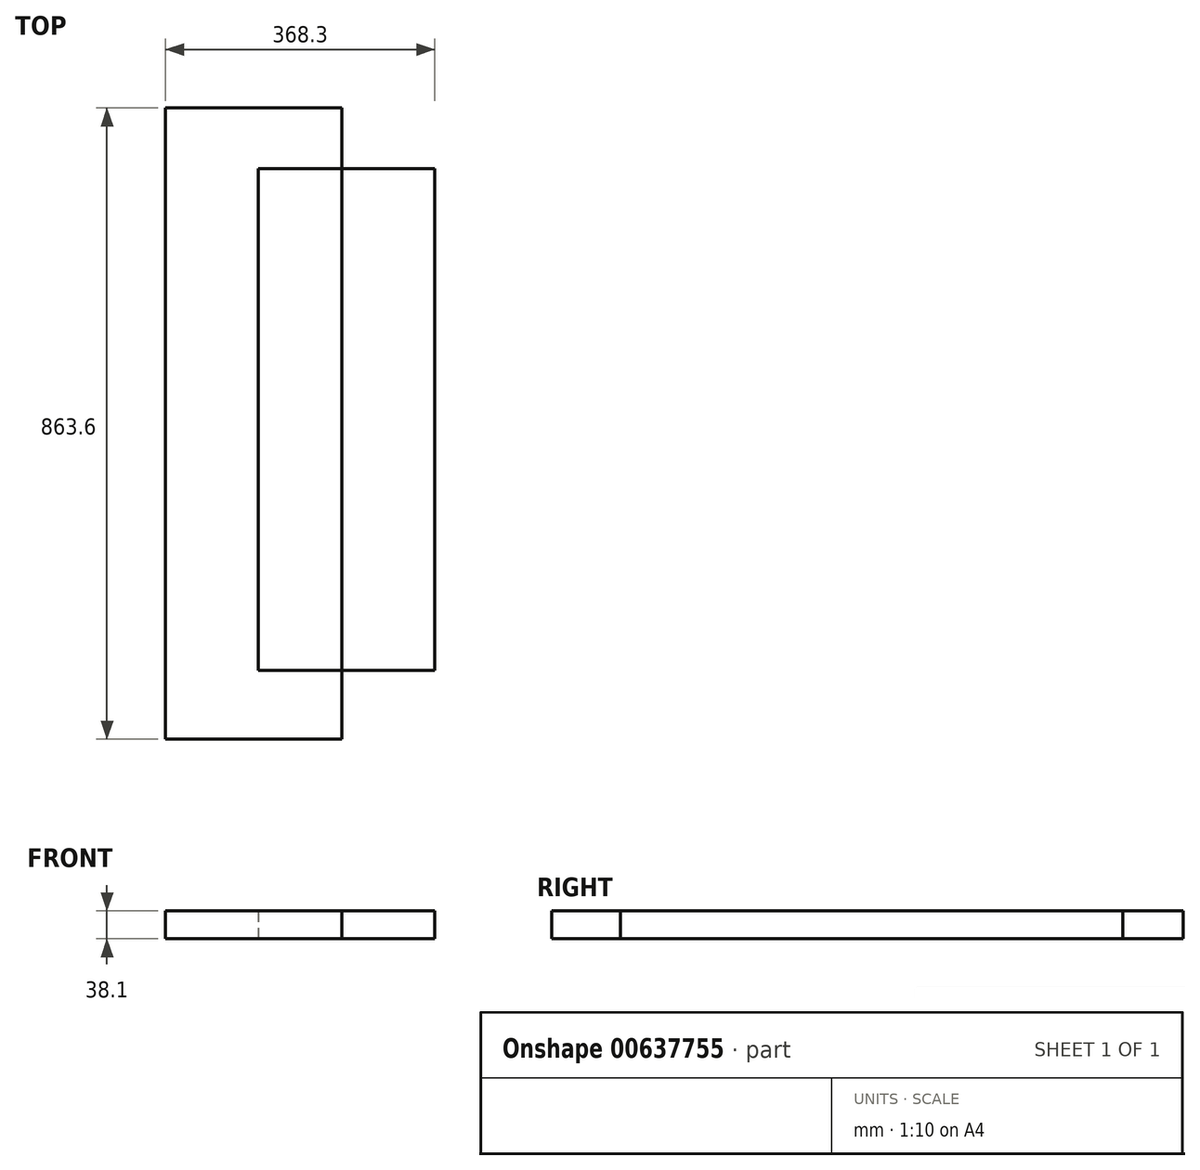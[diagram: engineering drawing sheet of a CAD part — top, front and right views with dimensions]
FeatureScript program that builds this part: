
annotation { "Feature Type Name" : "Feature", "Feature Type Description" : "" }
export const myFeature = defineFeature(function(context is Context, id is Id, definition is map)
    precondition{}
    {
        {
            var Q0;
            Q0=qCreatedBy(makeId("Top.planeOp"),FACE);
            var sketch = newSketch(context, id + "F0", { "sketchPlane" : qUnion([Q0])});
            skLineSegment(sketch, "E0.bottom", {"start": v(-122.87, 430.6) * mm, "end": v(4.13, 430.6) * mm});
            skLineSegment(sketch, "E0.top", {"start": v(-122.87, -433) * mm, "end": v(4.13, -433) * mm});
            skLineSegment(sketch, "E0.left", {"start": v(-122.87, 430.6) * mm, "end": v(-122.87, -433) * mm});
            skLineSegment(sketch, "E0.right", {"start": v(4.13, 430.6) * mm, "end": v(4.13, -433) * mm});
            skLineSegment(sketch, "E1.bottom", {"start": v(-122.87, -433) * mm, "end": v(245.43, -433) * mm});
            skLineSegment(sketch, "E1.top", {"start": v(-122.87, -339.02) * mm, "end": v(245.43, -339.02) * mm});
            skLineSegment(sketch, "E1.left", {"start": v(-122.87, -433) * mm, "end": v(-122.87, -339.02) * mm});
            skLineSegment(sketch, "E1.right", {"start": v(245.43, -433) * mm, "end": v(245.43, -339.02) * mm});
            skLineSegment(sketch, "E2.bottom", {"start": v(245.43, -433) * mm, "end": v(118.43, -433) * mm});
            skLineSegment(sketch, "E2.top", {"start": v(245.43, 430.6) * mm, "end": v(118.43, 430.6) * mm});
            skLineSegment(sketch, "E2.left", {"start": v(245.43, -433) * mm, "end": v(245.43, 430.6) * mm});
            skLineSegment(sketch, "E2.right", {"start": v(118.43, -433) * mm, "end": v(118.43, 430.6) * mm});
            skLineSegment(sketch, "E3.bottom", {"start": v(-122.87, 430.6) * mm, "end": v(245.43, 430.6) * mm});
            skLineSegment(sketch, "E3.top", {"start": v(-122.87, 347.87) * mm, "end": v(245.43, 347.87) * mm});
            skLineSegment(sketch, "E3.left", {"start": v(-122.87, 430.6) * mm, "end": v(-122.87, 347.87) * mm});
            skLineSegment(sketch, "E3.right", {"start": v(245.43, 430.6) * mm, "end": v(245.43, 347.87) * mm});
            skSolve(sketch);
        }
        {
            var Q0;
            {var subQ0=sQuery(id+"F0.wireOp",EDGE,"E0.left");Q0=makeQuery(id+"F0.imprint","IMPRINT",FACE,{"disambiguationData":[TD([[makeQuery(id+"F0.imprint","IMPRINT",EDGE,{"derivedFrom":subQ0}),1.0]])]});}
            var Q1;
            {var subQ5=sQuery(id+"F0.wireOp",EDGE,"E1.left");Q1=makeQuery(id+"F0.imprint","IMPRINT",FACE,{"disambiguationData":[TD([[makeQuery(id+"F0.imprint","IMPRINT",EDGE,{"derivedFrom":subQ5}),-1.0]])]});}
            var Q2;
            {var subQ0=sQuery(id+"F0.wireOp",EDGE,"E1.bottom");var subQ1=sQuery(id+"F0.wireOp",EDGE,"E0.right");var subQ2=makeQuery(id+"F0.imprint","INTERSECT",VERTEX,{"derivedFrom":[subQ1,subQ0]});Q2=makeQuery(id+"F0.imprint","IMPRINT",FACE,{"disambiguationData":[TD([[makeQuery(id+"F0.imprint","IMPRINT",EDGE,{"disambiguationData":[TD([[subQ2,1.0]])],"derivedFrom":subQ1}),1.0]])]});}
            var Q3;
            {var subQ5=sQuery(id+"F0.wireOp",EDGE,"E2.bottom");Q3=makeQuery(id+"F0.imprint","IMPRINT",FACE,{"disambiguationData":[TD([[makeQuery(id+"F0.imprint","IMPRINT",EDGE,{"derivedFrom":subQ5}),-1.0]])]});}
            var Q4;
            {var subQ0=sQuery(id+"F0.wireOp",EDGE,"E2.left");var subQ1=sQuery(id+"F0.wireOp",EDGE,"E1.top");var subQ2=makeQuery(id+"F0.imprint","INTERSECT",VERTEX,{"derivedFrom":[subQ1,subQ0]});Q4=makeQuery(id+"F0.imprint","IMPRINT",FACE,{"disambiguationData":[TD([[makeQuery(id+"F0.imprint","IMPRINT",EDGE,{"disambiguationData":[TD([[subQ2,1.0]])],"derivedFrom":subQ1}),1.0]])]});}
            var Q5;
            {var subQ5=sQuery(id+"F0.wireOp",EDGE,"E3.right");Q5=makeQuery(id+"F0.imprint","IMPRINT",FACE,{"disambiguationData":[TD([[makeQuery(id+"F0.imprint","IMPRINT",EDGE,{"derivedFrom":subQ5}),-1.0]])]});}
            var Q6;
            {var subQ0=sQuery(id+"F0.wireOp",EDGE,"E3.bottom");var subQ1=sQuery(id+"F0.wireOp",EDGE,"E0.right");var subQ2=makeQuery(id+"F0.imprint","INTERSECT",VERTEX,{"derivedFrom":[subQ1,subQ0]});Q6=makeQuery(id+"F0.imprint","IMPRINT",FACE,{"disambiguationData":[TD([[makeQuery(id+"F0.imprint","IMPRINT",EDGE,{"disambiguationData":[TD([[subQ2,-1.0]])],"derivedFrom":subQ1}),1.0]])]});}
            var Q7;
            {var subQ5=sQuery(id+"F0.wireOp",EDGE,"E3.left");Q7=makeQuery(id+"F0.imprint","IMPRINT",FACE,{"disambiguationData":[TD([[makeQuery(id+"F0.imprint","IMPRINT",EDGE,{"derivedFrom":subQ5}),1.0]])]});}
            extrude(context, id + "F1", {"entities" : qUnion([Q0, Q1, Q2, Q3, Q4, Q5, Q6, Q7]), "depth" : 38.1 * mm, "offsetDistance" : 25.4 * mm});
        }
    });
